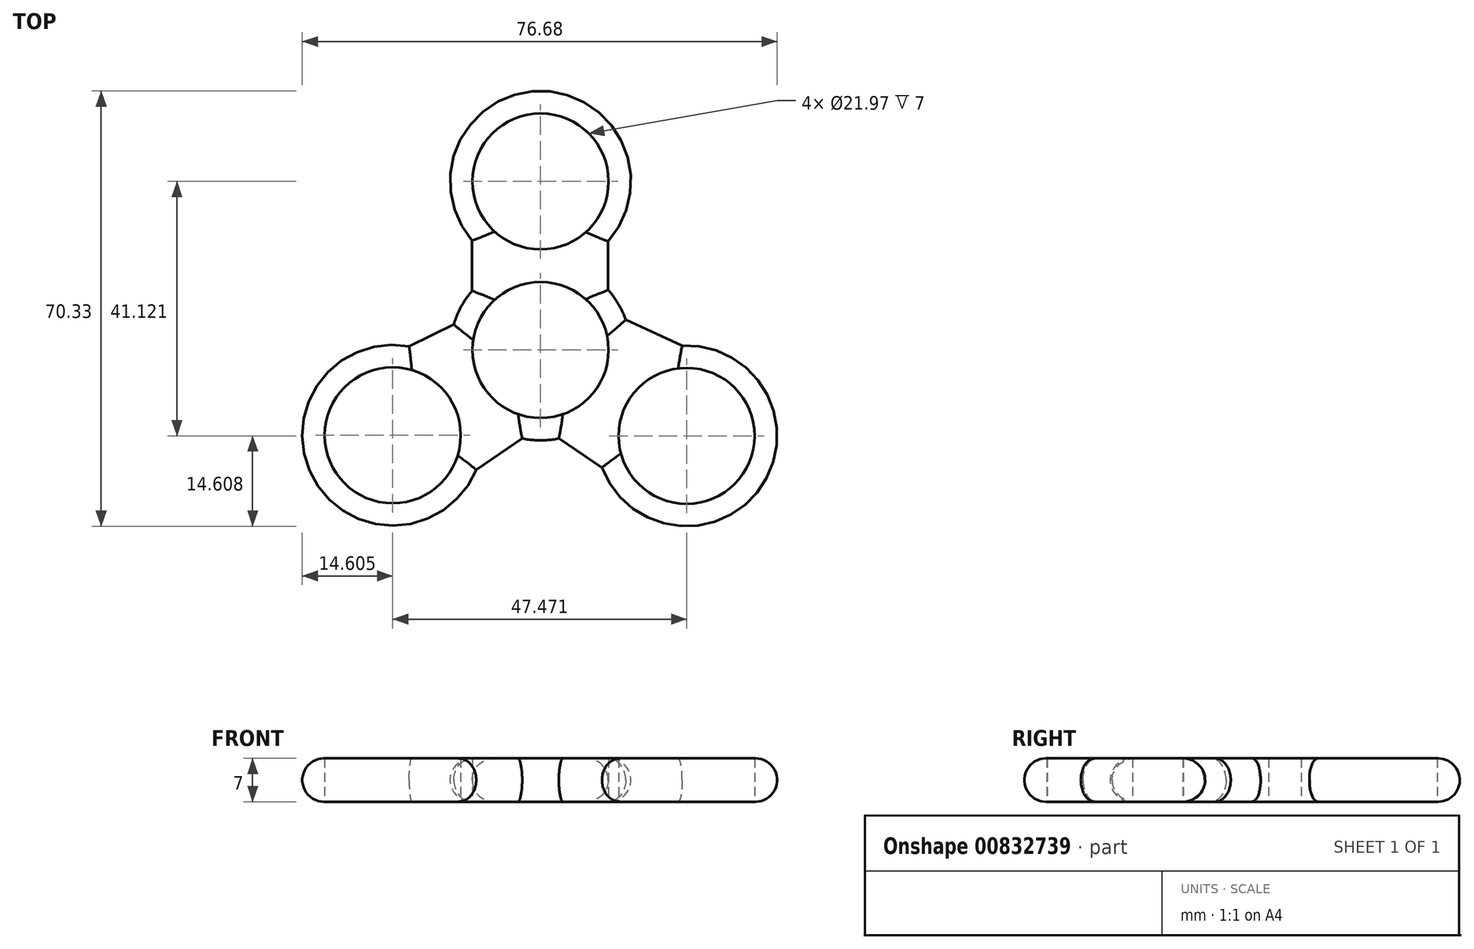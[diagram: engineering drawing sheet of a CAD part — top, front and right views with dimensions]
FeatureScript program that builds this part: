
annotation { "Feature Type Name" : "Feature", "Feature Type Description" : "" }
export const myFeature = defineFeature(function(context is Context, id is Id, definition is map)
    precondition{}
    {
        {
            var Q0;
            Q0=qCreatedBy(makeId("Top.planeOp"),FACE);
            var sketch = newSketch(context, id + "F0", { "sketchPlane" : qUnion([Q0])});
            skCircle(sketch, "E0", {"center": v(0, 0) * mm, "radius": 10.99 * mm});
            skArc(sketch, "E1", {"start": v(-11.04, 9.56) * mm, "mid": v(-12.82, 7) * mm, "end": v(-14.01, 4.12) * mm});
            skCircle(sketch, "E2", {"center": v(0, 27.24) * mm, "radius": 10.99 * mm});
            skArc(sketch, "E3", {"start": v(10.93, 17.55) * mm, "mid": v(0.09, 41.84) * mm, "end": v(-11.04, 17.68) * mm});
            skCircle(sketch, "E4", {"center": v(23.6, -13.88) * mm, "radius": 10.99 * mm});
            skArc(sketch, "E5", {"start": v(9.92, -19.01) * mm, "mid": v(35.8, -21.9) * mm, "end": v(22.87, 0.7) * mm});
            skCircle(sketch, "E6", {"center": v(-23.87, -13.78) * mm, "radius": 10.99 * mm});
            skArc(sketch, "E7", {"start": v(-21.22, 0.59) * mm, "mid": v(-36.7, -20.76) * mm, "end": v(-10.38, -19.35) * mm});
            skLineSegment(sketch, "E8", {"start": v(-11.04, 17.68) * mm, "end": v(-11.04, 9.56) * mm});
            skLineSegment(sketch, "E9", {"start": v(-14.01, 4.12) * mm, "end": v(-21.22, 0.59) * mm});
            skLineSegment(sketch, "E10", {"start": v(10.93, 17.55) * mm, "end": v(10.93, 9.7) * mm});
            skLineSegment(sketch, "E11", {"start": v(13.77, 4.87) * mm, "end": v(22.87, 0.7) * mm});
            skLineSegment(sketch, "E12", {"start": v(9.92, -19.01) * mm, "end": v(2.96, -14.3) * mm});
            skLineSegment(sketch, "E13", {"start": v(-2.96, -14.3) * mm, "end": v(-10.38, -19.35) * mm});
            skArc(sketch, "E14.trimOffspring", {"start": v(13.77, 4.87) * mm, "mid": v(12.58, 7.42) * mm, "end": v(10.93, 9.7) * mm});
            skArc(sketch, "E15.trimOffspring", {"start": v(-2.96, -14.3) * mm, "mid": v(0, -14.6) * mm, "end": v(2.96, -14.3) * mm});
            skSolve(sketch);
        }
        {
            var Q0;
            Q0 = qSketchRegion(id + "F0", true);
            extrude(context, id + "F1", {"entities" : qUnion([Q0]), "depth" : 7 * mm, "offsetDistance" : 25.4 * mm});
        }
        {
            var Q0;
            Q0=makeQuery(id+"F1.opExtrude","CAP_EDGE",EDGE,{"disambiguationData":[OSD([sQuery(id+"F0.wireOp",EDGE,"E3")])],"isStart":false});
            var Q1;
            Q1=makeQuery(id+"F1.opExtrude","CAP_EDGE",EDGE,{"disambiguationData":[OSD([sQuery(id+"F0.wireOp",EDGE,"E8")])],"isStart":false});
            var Q2;
            Q2=makeQuery(id+"F1.opExtrude","CAP_EDGE",EDGE,{"disambiguationData":[OSD([sQuery(id+"F0.wireOp",EDGE,"E1")])],"isStart":false});
            var Q3;
            Q3=makeQuery(id+"F1.opExtrude","CAP_EDGE",EDGE,{"disambiguationData":[OSD([sQuery(id+"F0.wireOp",EDGE,"E7")])],"isStart":false});
            var Q4;
            Q4=makeQuery(id+"F1.opExtrude","CAP_EDGE",EDGE,{"disambiguationData":[OSD([sQuery(id+"F0.wireOp",EDGE,"E9")])],"isStart":false});
            var Q5;
            Q5=makeQuery(id+"F1.opExtrude","CAP_EDGE",EDGE,{"disambiguationData":[OSD([sQuery(id+"F0.wireOp",EDGE,"E13")])],"isStart":false});
            var Q6;
            Q6=makeQuery(id+"F1.opExtrude","CAP_EDGE",EDGE,{"disambiguationData":[OSD([sQuery(id+"F0.wireOp",EDGE,"E15.trimOffspring")])],"isStart":false});
            var Q7;
            Q7=makeQuery(id+"F1.opExtrude","CAP_EDGE",EDGE,{"disambiguationData":[OSD([sQuery(id+"F0.wireOp",EDGE,"E12")])],"isStart":false});
            var Q8;
            Q8=makeQuery(id+"F1.opExtrude","CAP_EDGE",EDGE,{"disambiguationData":[OSD([sQuery(id+"F0.wireOp",EDGE,"E5")])],"isStart":false});
            var Q9;
            Q9=makeQuery(id+"F1.opExtrude","CAP_EDGE",EDGE,{"disambiguationData":[OSD([sQuery(id+"F0.wireOp",EDGE,"E11")])],"isStart":false});
            var Q10;
            Q10=makeQuery(id+"F1.opExtrude","CAP_EDGE",EDGE,{"disambiguationData":[OSD([sQuery(id+"F0.wireOp",EDGE,"E14.trimOffspring")])],"isStart":false});
            var Q11;
            Q11=makeQuery(id+"F1.opExtrude","CAP_EDGE",EDGE,{"disambiguationData":[OSD([sQuery(id+"F0.wireOp",EDGE,"E10")])],"isStart":false});
            fillet(context, id + "F2", {"entities" : qUnion([Q0, Q1, Q2, Q3, Q4, Q5, Q6, Q7, Q8, Q9, Q10, Q11]), "radius" : 3.5 * mm, "tangentPropagation" : true, "allowEdgeOverflow" : false});
        }
        {
            var Q0;
            Q0=makeQuery(id+"F1.opExtrude","CAP_EDGE",EDGE,{"disambiguationData":[OSD([sQuery(id+"F0.wireOp",EDGE,"E3")])],"isStart":true});
            var Q1;
            Q1=makeQuery(id+"F1.opExtrude","CAP_EDGE",EDGE,{"disambiguationData":[OSD([sQuery(id+"F0.wireOp",EDGE,"E10")])],"isStart":true});
            var Q2;
            Q2=makeQuery(id+"F1.opExtrude","CAP_EDGE",EDGE,{"disambiguationData":[OSD([sQuery(id+"F0.wireOp",EDGE,"E14.trimOffspring")])],"isStart":true});
            var Q3;
            Q3=makeQuery(id+"F1.opExtrude","CAP_EDGE",EDGE,{"disambiguationData":[OSD([sQuery(id+"F0.wireOp",EDGE,"E11")])],"isStart":true});
            var Q4;
            Q4=makeQuery(id+"F1.opExtrude","CAP_EDGE",EDGE,{"disambiguationData":[OSD([sQuery(id+"F0.wireOp",EDGE,"E5")])],"isStart":true});
            var Q5;
            Q5=makeQuery(id+"F1.opExtrude","CAP_EDGE",EDGE,{"disambiguationData":[OSD([sQuery(id+"F0.wireOp",EDGE,"E12")])],"isStart":true});
            var Q6;
            Q6=makeQuery(id+"F1.opExtrude","CAP_EDGE",EDGE,{"disambiguationData":[OSD([sQuery(id+"F0.wireOp",EDGE,"E15.trimOffspring")])],"isStart":true});
            var Q7;
            Q7=makeQuery(id+"F1.opExtrude","CAP_EDGE",EDGE,{"disambiguationData":[OSD([sQuery(id+"F0.wireOp",EDGE,"E13")])],"isStart":true});
            var Q8;
            Q8=makeQuery(id+"F1.opExtrude","CAP_EDGE",EDGE,{"disambiguationData":[OSD([sQuery(id+"F0.wireOp",EDGE,"E7")])],"isStart":true});
            var Q9;
            Q9=makeQuery(id+"F1.opExtrude","CAP_EDGE",EDGE,{"disambiguationData":[OSD([sQuery(id+"F0.wireOp",EDGE,"E9")])],"isStart":true});
            var Q10;
            Q10=makeQuery(id+"F1.opExtrude","CAP_EDGE",EDGE,{"disambiguationData":[OSD([sQuery(id+"F0.wireOp",EDGE,"E1")])],"isStart":true});
            var Q11;
            Q11=makeQuery(id+"F1.opExtrude","CAP_EDGE",EDGE,{"disambiguationData":[OSD([sQuery(id+"F0.wireOp",EDGE,"E8")])],"isStart":true});
            fillet(context, id + "F3", {"entities" : qUnion([Q0, Q1, Q2, Q3, Q4, Q5, Q6, Q7, Q8, Q9, Q10, Q11]), "radius" : 3.5 * mm, "tangentPropagation" : true, "allowEdgeOverflow" : false});
        }
    });
